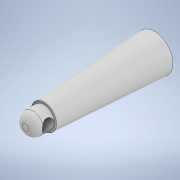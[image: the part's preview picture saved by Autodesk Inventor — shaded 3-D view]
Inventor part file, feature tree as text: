
AUTODESK INVENTOR PART (.ipt)
format: ipt  version: 2021 (Build 250183000, 183)  size: 134,656 bytes
history: native  units: mm
features: extrude x3, sketch x3, fillet x1
ambient origin geometry x8: Origin, YZ Plane, XZ Plane, XY Plane, X Axis, Y Axis, Z Axis, Center Point
bodies: Solid1 (feature_tree)
feature tree (7):
  extrude  "Extrusion1"  Depth=30.0mm
  extrude  "Extrusion2"  Depth=2.0mm
  fillet  "Fillet1"  [1 undecoded]
  extrude  "Extrusion3"  [1 undecoded]
  sketch  "Sketch1"  dims[d0=10.0mm d1=30.0mm d2=-0.523599mm]
  sketch  "Sketch2"  dims[d3=5.0mm d4=0.0mm d5=2.0mm d6=0.0mm d7=0.0mm]
  sketch  "Sketch3"
note: 2 required parameter values undecoded (feature->parameter linkage not recoverable at this tier; creation-order binding heuristic only, values carry confidence <= 0.55)
